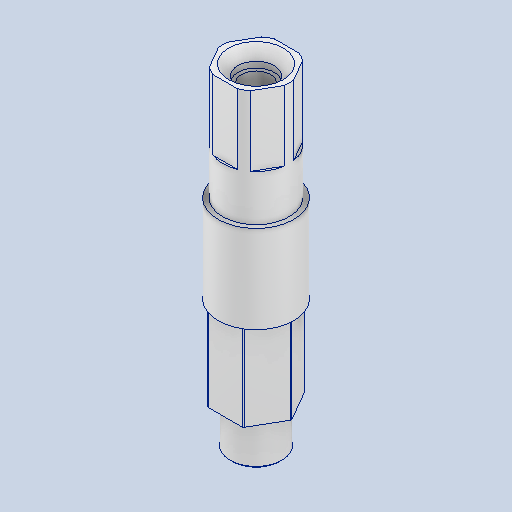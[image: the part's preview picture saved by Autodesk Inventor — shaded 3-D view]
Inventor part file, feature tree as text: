
AUTODESK INVENTOR PART (.ipt)
format: ipt  version: 2024 (Build 280153000, 153)  size: 136,192 bytes
history: native  units: in
note: dims shown in document units (in); Inventor stores cm internally (conversion verified against a paired STEP export)
features: fillet x1
ambient origin geometry x8: Origin, YZ Plane, XZ Plane, XY Plane, X Axis, Y Axis, Z Axis, Center Point
bodies: Solid1 (feature_tree)
feature tree (1):
  fillet  "Fillet1"  [1 undecoded]
note: 1 required parameter value undecoded (feature->parameter linkage not recoverable at this tier; creation-order binding heuristic only, values carry confidence <= 0.55)
